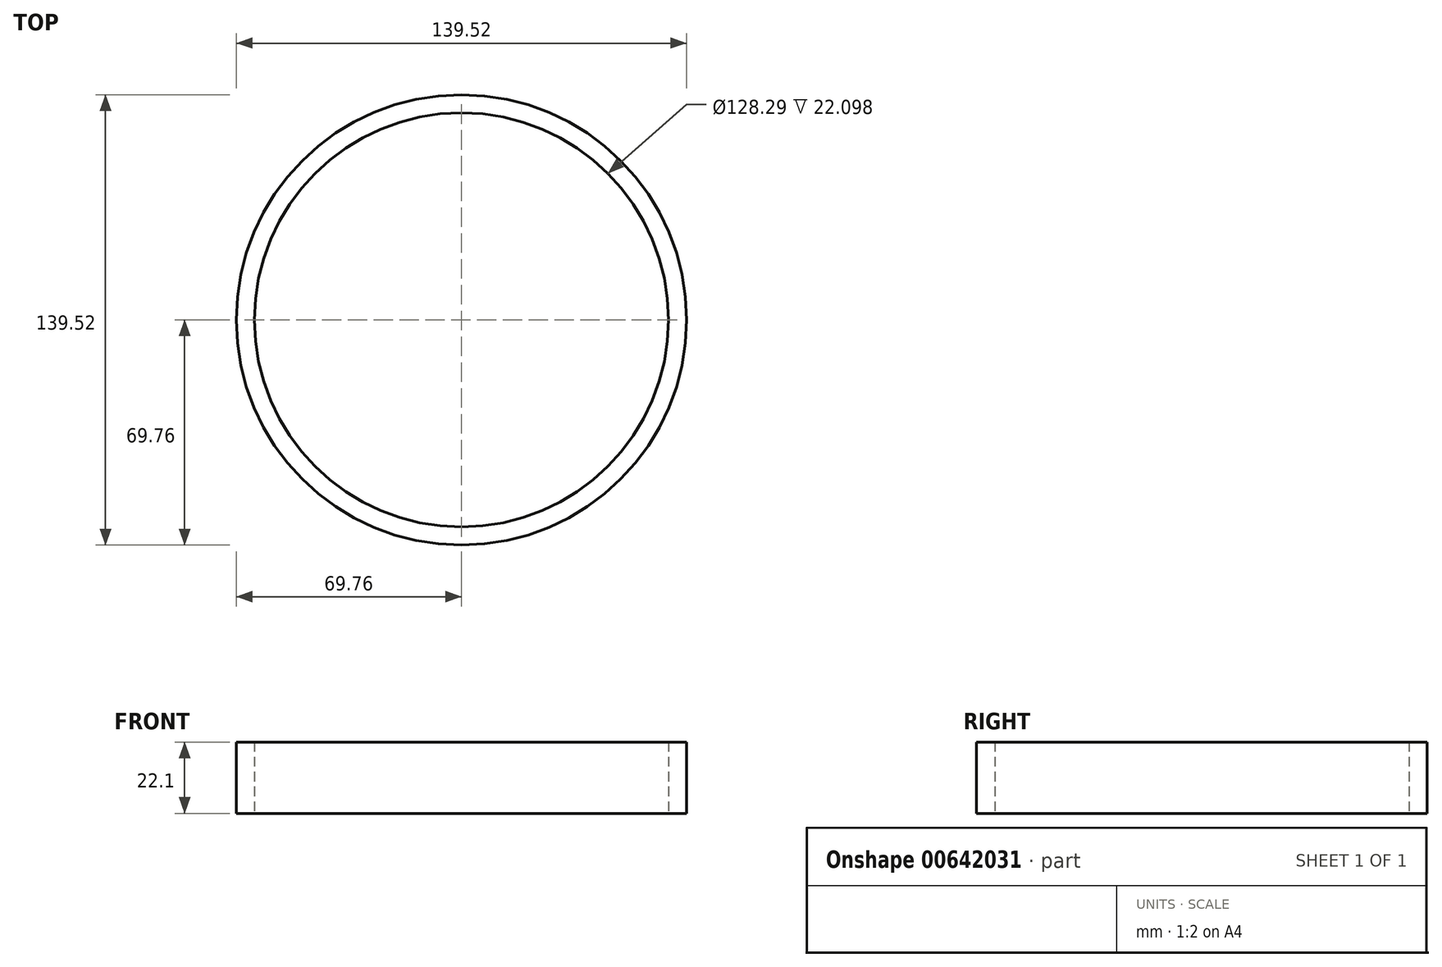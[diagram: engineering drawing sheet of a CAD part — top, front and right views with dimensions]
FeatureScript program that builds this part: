
annotation { "Feature Type Name" : "Feature", "Feature Type Description" : "" }
export const myFeature = defineFeature(function(context is Context, id is Id, definition is map)
    precondition{}
    {
        {
            var Q0;
            Q0=qCreatedBy(makeId("Top.planeOp"),FACE);
            var sketch = newSketch(context, id + "F0", { "sketchPlane" : qUnion([Q0])});
            skCircle(sketch, "E0", {"center": v(0, 0) * mm, "radius": 69.76 * mm});
            skSolve(sketch);
        }
        {
            var Q0;
            Q0=qCreatedBy(makeId("Top.planeOp"),FACE);
            var sketch = newSketch(context, id + "F1", { "sketchPlane" : qUnion([Q0])});
            skCircle(sketch, "E1", {"center": v(0, 0) * mm, "radius": 64.14 * mm});
            skSolve(sketch);
        }
        {
            var Q0;
            Q0=makeQuery(id+"F0.imprint","IMPRINT",FACE,{"disambiguationData":[TD([[makeQuery(id+"F0.imprint","IMPRINT",EDGE,{"derivedFrom":sQuery(id+"F0.wireOp",EDGE,"E0")}),1.0]])]});
            extrude(context, id + "F2", {"entities" : qUnion([Q0]), "depth" : 22.1 * mm, "offsetDistance" : 25.4 * mm});
        }
        {
            var Q0;
            Q0=makeQuery(id+"F1.imprint","IMPRINT",FACE,{"disambiguationData":[TD([[makeQuery(id+"F1.imprint","IMPRINT",EDGE,{"derivedFrom":sQuery(id+"F1.wireOp",EDGE,"E1")}),1.0]])]});
            extrude(context, id + "F3", {"entities" : qUnion([Q0]), "operationType" : NewBodyOperationType.REMOVE, "depth" : 38.6 * mm, "offsetDistance" : 25.4 * mm});
        }
    });
